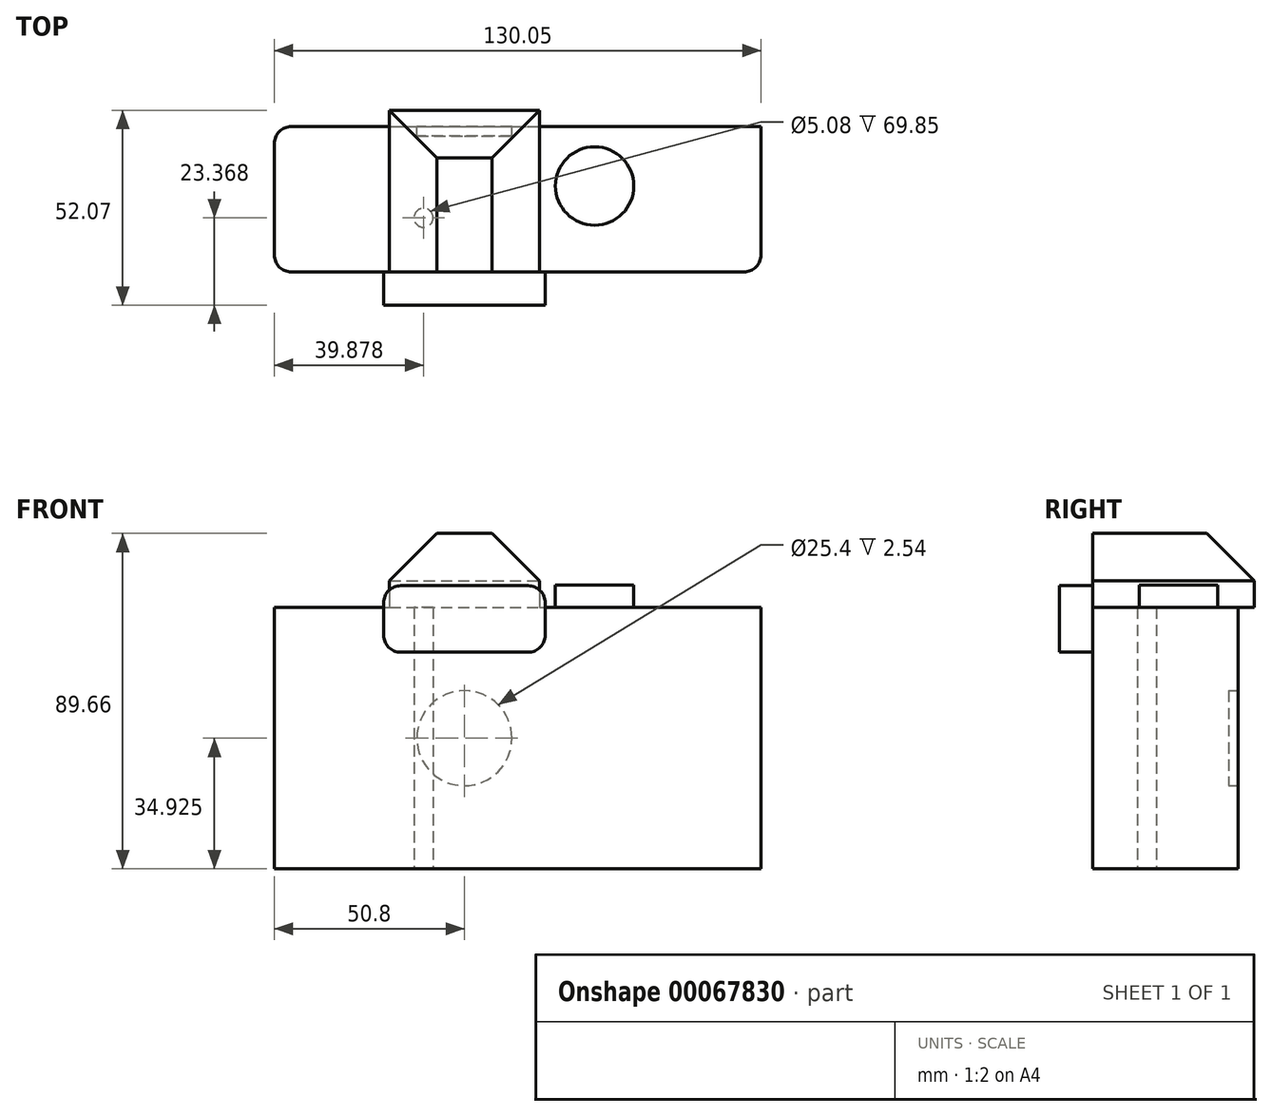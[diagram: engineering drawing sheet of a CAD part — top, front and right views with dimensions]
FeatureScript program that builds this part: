
annotation { "Feature Type Name" : "Feature", "Feature Type Description" : "" }
export const myFeature = defineFeature(function(context is Context, id is Id, definition is map)
    precondition{}
    {
        {
            var Q0;
            Q0=qCreatedBy(makeId("Top.planeOp"),FACE);
            var sketch = newSketch(context, id + "F0", { "sketchPlane" : qUnion([Q0])});
            skLineSegment(sketch, "E0.bottom", {"start": v(4.57, 0) * mm, "end": v(125.48, 0) * mm});
            skLineSegment(sketch, "E0.top", {"start": v(4.57, 38.86) * mm, "end": v(130.05, 38.86) * mm});
            skLineSegment(sketch, "E0.left", {"start": v(0, 4.57) * mm, "end": v(0, 34.3) * mm});
            skLineSegment(sketch, "E0.right", {"start": v(130.05, 4.57) * mm, "end": v(130.05, 38.86) * mm});
            skCircle(sketch, "E1", {"center": v(39.88, 14.48) * mm, "radius": 2.54 * mm});
            skPoint(sketch, "E2.visualSharp", {"position": v(0, 0) * mm});
            skArc(sketch, "E2.filletArc", {"start": v(0, 4.57) * mm, "mid": v(1.34, 1.34) * mm, "end": v(4.57, 0) * mm});
            skPoint(sketch, "E3.visualSharp", {"position": v(0, 38.86) * mm});
            skArc(sketch, "E3.filletArc", {"start": v(4.57, 38.86) * mm, "mid": v(1.34, 37.52) * mm, "end": v(0, 34.3) * mm});
            skPoint(sketch, "E4.visualSharp", {"position": v(130.05, 0) * mm});
            skArc(sketch, "E4.filletArc", {"start": v(125.48, 0) * mm, "mid": v(128.7, 1.34) * mm, "end": v(130.05, 4.57) * mm});
            skLineSegment(sketch, "E5.bottom", {"start": v(130.05, 38.86) * mm, "end": v(96.01, 38.86) * mm});
            skLineSegment(sketch, "E5.top", {"start": v(114.05, 73.58) * mm, "end": v(108.22, 73.58) * mm});
            skLineSegment(sketch, "E5.left", {"start": v(130.05, 38.86) * mm, "end": v(130.05, 57.58) * mm});
            skLineSegment(sketch, "E5.right", {"start": v(96.01, 38.86) * mm, "end": v(103.79, 70.11) * mm});
            skPoint(sketch, "E6.visualSharp", {"position": v(104.65, 73.58) * mm});
            skArc(sketch, "E6.filletArc", {"start": v(108.22, 73.58) * mm, "mid": v(105.4, 72.61) * mm, "end": v(103.79, 70.11) * mm});
            skPoint(sketch, "E7.visualSharp", {"position": v(130.05, 73.58) * mm});
            skArc(sketch, "E7.filletArc", {"start": v(130.05, 57.58) * mm, "mid": v(125.36, 68.9) * mm, "end": v(114.05, 73.58) * mm});
            skSolve(sketch);
        }
        {
            var Q0;
            Q0=makeQuery(id+"F0.imprint","IMPRINT",FACE,{"disambiguationData":[TD([[makeQuery(id+"F0.imprint","IMPRINT",EDGE,{"derivedFrom":sQuery(id+"F0.wireOp",EDGE,"E5.bottom")}),-1.0]])]});
            var Q1;
            Q1=makeQuery(id+"F0.imprint","IMPRINT",FACE,{"disambiguationData":[TD([[makeQuery(id+"F0.imprint","IMPRINT",EDGE,{"derivedFrom":sQuery(id+"F0.wireOp",EDGE,"E0.bottom")}),1.0]])]});
            extrude(context, id + "F1", {"entities" : qUnion([Q0, Q1]), "depth" : 69.85 * mm});
        }
        {
            var Q0;
            Q0=makeQuery(id+"F1.opExtrude","CAP_FACE",FACE,{"disambiguationData":[OSD([sQuery(id+"F0.wireOp",EDGE,"E0.bottom"),sQuery(id+"F0.wireOp",EDGE,"E0.top"),sQuery(id+"F0.wireOp",EDGE,"E0.left"),sQuery(id+"F0.wireOp",EDGE,"E0.right"),sQuery(id+"F0.wireOp",EDGE,"E1"),sQuery(id+"F0.wireOp",EDGE,"E2.filletArc"),sQuery(id+"F0.wireOp",EDGE,"E3.filletArc"),sQuery(id+"F0.wireOp",EDGE,"E4.filletArc"),sQuery(id+"F0.wireOp",EDGE,"E5.top"),sQuery(id+"F0.wireOp",EDGE,"E5.left"),sQuery(id+"F0.wireOp",EDGE,"E5.right"),sQuery(id+"F0.wireOp",EDGE,"E6.filletArc"),sQuery(id+"F0.wireOp",EDGE,"E7.filletArc")])],"isStart":false});
            var sketch = newSketch(context, id + "F2", { "sketchPlane" : qUnion([Q0])});
            skLineSegment(sketch, "E8.bottom", {"start": v(30.73, 43.18) * mm, "end": v(70.87, 43.18) * mm});
            skLineSegment(sketch, "E8.top", {"start": v(30.73, 0) * mm, "end": v(70.87, 0) * mm});
            skLineSegment(sketch, "E8.left", {"start": v(30.73, 43.18) * mm, "end": v(30.73, 0) * mm});
            skLineSegment(sketch, "E8.right", {"start": v(70.87, 43.18) * mm, "end": v(70.87, 0) * mm});
            skSolve(sketch);
        }
        {
            var Q0;
            Q0=makeQuery(id+"F2.imprint","IMPRINT",FACE,{"disambiguationData":[TD([[makeQuery(id+"F2.imprint","IMPRINT",EDGE,{"derivedFrom":makeQuery(id+"F1.opExtrude","CAP_EDGE",EDGE,{"disambiguationData":[OSD([sQuery(id+"F0.wireOp",EDGE,"E1")])],"isStart":false})}),1.0]])]});
            var Q1;
            {var subQ0=sQuery(id+"F2.wireOp",EDGE,"E8.bottom");Q1=makeQuery(id+"F2.imprint","IMPRINT",FACE,{"disambiguationData":[TD([[makeQuery(id+"F2.imprint","IMPRINT",EDGE,{"derivedFrom":subQ0}),-1.0]])]});}
            var Q2;
            {var subQ1=sQuery(id+"F2.wireOp",EDGE,"E8.top");Q2=makeQuery(id+"F2.imprint","IMPRINT",FACE,{"disambiguationData":[TD([[makeQuery(id+"F2.imprint","IMPRINT",EDGE,{"derivedFrom":subQ1}),1.0]])]});}
            extrude(context, id + "F3", {"entities" : qUnion([Q0, Q1, Q2]), "operationType" : NewBodyOperationType.ADD, "depth" : 19.8 * mm});
        }
        {
            var Q0;
            Q0=makeQuery(id+"F3.opExtrude","CAP_EDGE",EDGE,{"disambiguationData":[OSD([sQuery(id+"F2.wireOp",EDGE,"E8.right")])],"isStart":false});
            var Q1;
            Q1=makeQuery(id+"F3.opExtrude","CAP_EDGE",EDGE,{"disambiguationData":[OSD([sQuery(id+"F2.wireOp",EDGE,"E8.bottom")])],"isStart":false});
            var Q2;
            Q2=makeQuery(id+"F3.opExtrude","CAP_EDGE",EDGE,{"disambiguationData":[OSD([sQuery(id+"F2.wireOp",EDGE,"E8.left")])],"isStart":false});
            chamfer(context, id + "F4", {"entities" : qUnion([Q0, Q1, Q2]), "width" : 12.7 * mm, "tangentPropagation" : true});
        }
        {
            var Q0;
            Q0=qCreatedBy(makeId("Front.planeOp"),FACE);
            var sketch = newSketch(context, id + "F5", { "sketchPlane" : qUnion([Q0])});
            skLineSegment(sketch, "E9.bottom", {"start": v(33.78, 57.91) * mm, "end": v(67.82, 57.91) * mm});
            skLineSegment(sketch, "E9.top", {"start": v(33.78, 75.7) * mm, "end": v(67.82, 75.7) * mm});
            skLineSegment(sketch, "E9.left", {"start": v(29.21, 62.48) * mm, "end": v(29.21, 71.12) * mm});
            skLineSegment(sketch, "E9.right", {"start": v(72.4, 62.48) * mm, "end": v(72.4, 71.12) * mm});
            skPoint(sketch, "E10.visualSharp", {"position": v(29.21, 75.7) * mm});
            skArc(sketch, "E10.filletArc", {"start": v(33.78, 75.7) * mm, "mid": v(30.55, 74.35) * mm, "end": v(29.21, 71.12) * mm});
            skPoint(sketch, "E11.visualSharp", {"position": v(72.4, 75.7) * mm});
            skArc(sketch, "E11.filletArc", {"start": v(72.4, 71.12) * mm, "mid": v(71.05, 74.35) * mm, "end": v(67.82, 75.7) * mm});
            skPoint(sketch, "E12.visualSharp", {"position": v(72.4, 57.91) * mm});
            skArc(sketch, "E12.filletArc", {"start": v(67.82, 57.91) * mm, "mid": v(71.05, 59.25) * mm, "end": v(72.4, 62.48) * mm});
            skPoint(sketch, "E13.visualSharp", {"position": v(29.21, 57.91) * mm});
            skArc(sketch, "E13.filletArc", {"start": v(29.21, 62.48) * mm, "mid": v(30.55, 59.25) * mm, "end": v(33.78, 57.91) * mm});
            skSolve(sketch);
        }
        {
            var Q0;
            Q0=makeQuery(id+"F5.imprint","IMPRINT",FACE,{"disambiguationData":[TD([[makeQuery(id+"F5.imprint","IMPRINT",EDGE,{"derivedFrom":sQuery(id+"F5.wireOp",EDGE,"E9.bottom")}),1.0]])]});
            var Q1;
            Q1=makeQuery(id+"F1.opExtrude","SWEPT_FACE",FACE,{"disambiguationData":[OSD([sQuery(id+"F0.wireOp",EDGE,"E0.top")])]});
            extrude(context, id + "F6", {"entities" : qUnion([Q0, Q1]), "operationType" : NewBodyOperationType.ADD, "depth" : 8.9 * mm});
        }
        {
            var Q0;
            {var subQ2=sQuery(id+"F0.wireOp",EDGE,"E7.filletArc");var subQ3=sQuery(id+"F0.wireOp",EDGE,"E5.right");var subQ4=sQuery(id+"F0.wireOp",EDGE,"E0.bottom");var subQ5=sQuery(id+"F0.wireOp",EDGE,"E5.top");var subQ6=sQuery(id+"F0.wireOp",EDGE,"E0.top");var subQ7=sQuery(id+"F0.wireOp",EDGE,"E4.filletArc");var subQ8=sQuery(id+"F0.wireOp",EDGE,"E6.filletArc");var subQ9=sQuery(id+"F0.wireOp",EDGE,"E5.left");var subQ10=sQuery(id+"F0.wireOp",EDGE,"E0.right");Q0=makeQuery(id+"F3.boolean.opBoolean","SPLIT",FACE,{"disambiguationData":[TD([makeQuery(id+"F1.opExtrude","SWEPT_FACE",FACE,{"disambiguationData":[OSD([subQ7])]})])],"derivedFrom":makeQuery(id+"F1.opExtrude","CAP_FACE",FACE,{"disambiguationData":[OSD([subQ4,subQ6,sQuery(id+"F0.wireOp",EDGE,"E0.left"),subQ10,sQuery(id+"F0.wireOp",EDGE,"E1"),sQuery(id+"F0.wireOp",EDGE,"E2.filletArc"),sQuery(id+"F0.wireOp",EDGE,"E3.filletArc"),subQ7,subQ5,subQ9,subQ3,subQ8,subQ2])],"isStart":false})});}
            var sketch = newSketch(context, id + "F7", { "sketchPlane" : qUnion([Q0])});
            skCircle(sketch, "E14", {"center": v(85.6, 22.99) * mm, "radius": 10.48 * mm});
            skSolve(sketch);
        }
        {
            var Q0;
            Q0 = qSketchRegion(id + "F7", true);
            extrude(context, id + "F8", {"entities" : qUnion([Q0]), "operationType" : NewBodyOperationType.ADD, "depth" : 5.97 * mm});
        }
        {
            var Q0;
            Q0=makeQuery(id+"F1.opExtrude","SWEPT_FACE",FACE,{"disambiguationData":[OSD([sQuery(id+"F0.wireOp",EDGE,"E0.top")])]});
            var sketch = newSketch(context, id + "F9", { "sketchPlane" : qUnion([Q0])});
            skCircle(sketch, "E15", {"center": v(-50.8, 34.92) * mm, "radius": 12.7 * mm});
            skSolve(sketch);
        }
        {
            var Q0;
            Q0 = qSketchRegion(id + "F9", true);
            extrude(context, id + "F10", {"entities" : qUnion([Q0]), "operationType" : NewBodyOperationType.REMOVE, "oppositeDirection" : true, "depth" : 2.54 * mm});
        }
    });
